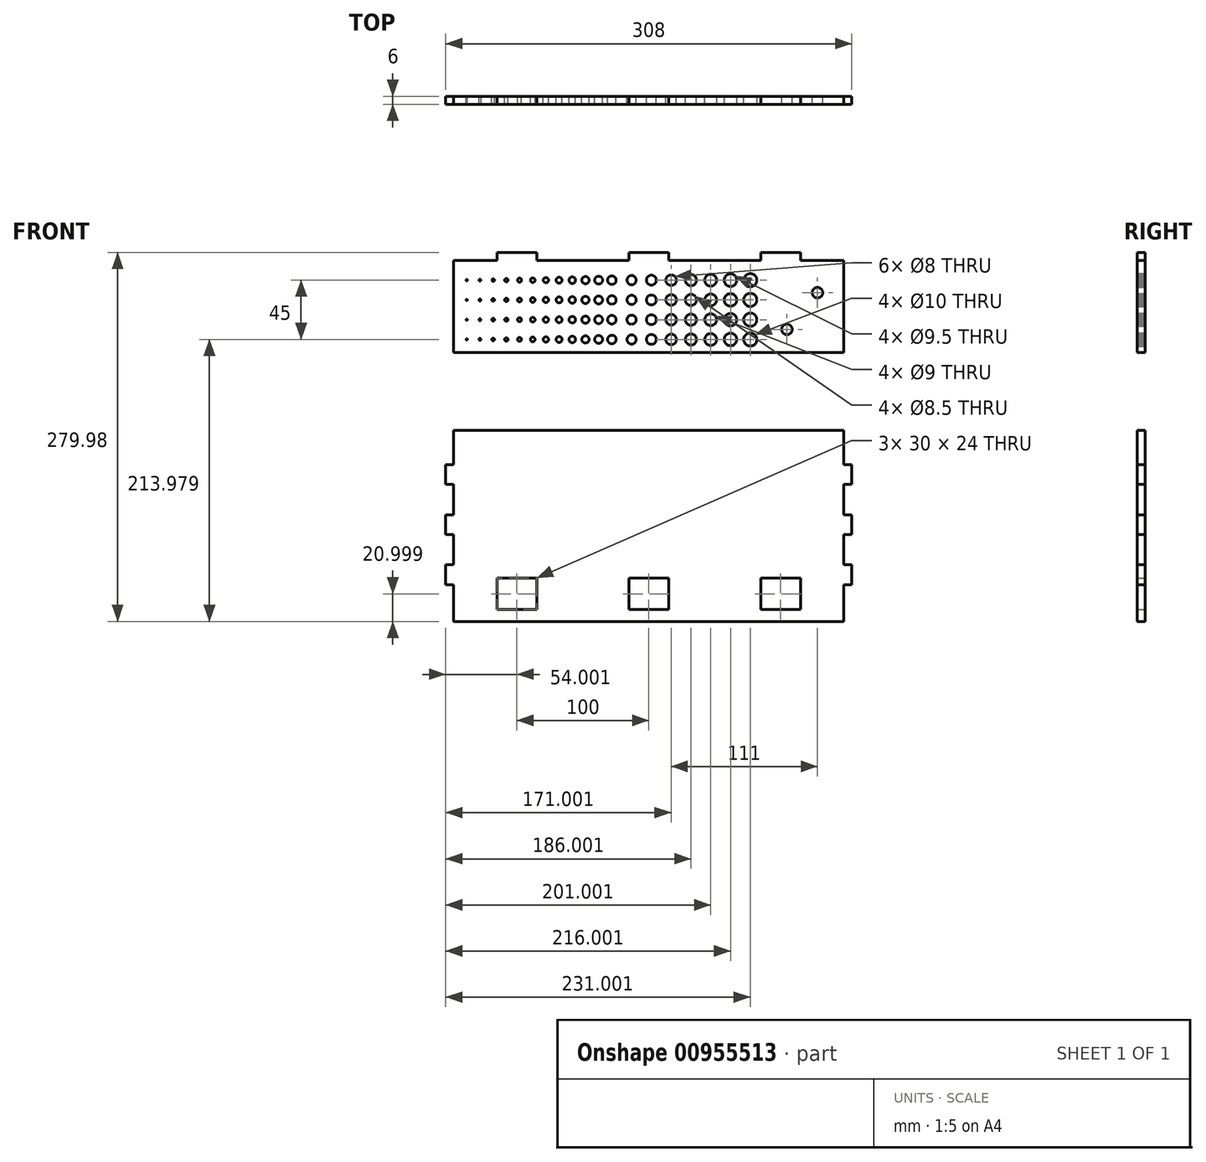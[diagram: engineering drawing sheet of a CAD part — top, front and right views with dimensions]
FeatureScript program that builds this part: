
annotation { "Feature Type Name" : "Feature", "Feature Type Description" : "" }
export const myFeature = defineFeature(function(context is Context, id is Id, definition is map)
    precondition{}
    {
        {
            var Q0;
            Q0=qCreatedBy(makeId("Front.planeOp"),FACE);
            var sketch = newSketch(context, id + "F0", { "sketchPlane" : qUnion([Q0])});
            skLineSegment(sketch, "E0", {"start": v(-100.8, -16.21) * mm, "end": v(195.2, -16.21) * mm, "construction": true});
            skPoint(sketch, "E1", {"position": v(-90.8, -16.21) * mm});
            skPoint(sketch, "E2.1.0.0", {"position": v(-80.8, -16.21) * mm});
            skPoint(sketch, "E2.2.0.0", {"position": v(-70.8, -16.21) * mm});
            skPoint(sketch, "E2.3.0.0", {"position": v(-60.8, -16.21) * mm});
            skPoint(sketch, "E2.4.0.0", {"position": v(-50.8, -16.21) * mm});
            skPoint(sketch, "E2.5.0.0", {"position": v(-40.8, -16.21) * mm});
            skPoint(sketch, "E2.6.0.0", {"position": v(-30.8, -16.21) * mm});
            skPoint(sketch, "E2.7.0.0", {"position": v(-20.8, -16.21) * mm});
            skPoint(sketch, "E2.8.0.0", {"position": v(-10.8, -16.21) * mm});
            skPoint(sketch, "E2.9.0.0", {"position": v(-0.8, -16.21) * mm});
            skPoint(sketch, "E2.10.0.0", {"position": v(9.2, -16.21) * mm});
            skPoint(sketch, "E2.11.0.0", {"position": v(19.2, -16.21) * mm});
            skLineSegment(sketch, "E2.direction1", {"start": v(-90.8, -16.21) * mm, "end": v(-80.8, -16.21) * mm, "construction": true});
            skPoint(sketch, "E3", {"position": v(34.2, -16.21) * mm});
            skPoint(sketch, "E4.1.0.0", {"position": v(49.2, -16.21) * mm});
            skPoint(sketch, "E4.2.0.0", {"position": v(64.2, -16.21) * mm});
            skPoint(sketch, "E4.3.0.0", {"position": v(79.2, -16.21) * mm});
            skPoint(sketch, "E4.4.0.0", {"position": v(94.2, -16.21) * mm});
            skPoint(sketch, "E4.5.0.0", {"position": v(109.2, -16.21) * mm});
            skPoint(sketch, "E4.6.0.0", {"position": v(124.2, -16.21) * mm});
            skLineSegment(sketch, "E4.direction1", {"start": v(34.2, -16.21) * mm, "end": v(49.2, -16.21) * mm, "construction": true});
            skCircle(sketch, "E5", {"center": v(-90.8, -16.21) * mm, "radius": 0.5 * mm});
            skCircle(sketch, "E6", {"center": v(-80.8, -16.21) * mm, "radius": 0.75 * mm});
            skCircle(sketch, "E7", {"center": v(-70.8, -16.21) * mm, "radius": 1 * mm});
            skCircle(sketch, "E8", {"center": v(-60.8, -16.21) * mm, "radius": 1.25 * mm});
            skCircle(sketch, "E9", {"center": v(-50.8, -16.21) * mm, "radius": 1.5 * mm});
            skCircle(sketch, "E10", {"center": v(-40.8, -16.21) * mm, "radius": 1.75 * mm});
            skCircle(sketch, "E11", {"center": v(-30.8, -16.21) * mm, "radius": 2 * mm});
            skCircle(sketch, "E12", {"center": v(-20.8, -16.21) * mm, "radius": 2.25 * mm});
            skCircle(sketch, "E13", {"center": v(-10.8, -16.21) * mm, "radius": 2.5 * mm});
            skCircle(sketch, "E14", {"center": v(-0.8, -16.21) * mm, "radius": 2.75 * mm});
            skCircle(sketch, "E15", {"center": v(9.2, -16.21) * mm, "radius": 3 * mm});
            skCircle(sketch, "E16", {"center": v(19.2, -16.21) * mm, "radius": 3.25 * mm});
            skCircle(sketch, "E17", {"center": v(34.2, -16.21) * mm, "radius": 3.5 * mm});
            skCircle(sketch, "E18", {"center": v(49.2, -16.21) * mm, "radius": 3.75 * mm});
            skCircle(sketch, "E19", {"center": v(64.2, -16.21) * mm, "radius": 4 * mm});
            skCircle(sketch, "E20", {"center": v(79.2, -16.21) * mm, "radius": 4.25 * mm});
            skCircle(sketch, "E21", {"center": v(94.2, -16.21) * mm, "radius": 4.5 * mm});
            skCircle(sketch, "E22", {"center": v(109.2, -16.21) * mm, "radius": 4.75 * mm});
            skCircle(sketch, "E23", {"center": v(124.2, -16.21) * mm, "radius": 5 * mm});
            skCircle(sketch, "E24", {"center": v(175.2, 19.28) * mm, "radius": 4 * mm});
            skCircle(sketch, "E25", {"center": v(175.2, 19.28) * mm, "radius": 15 * mm, "construction": true});
            skPoint(sketch, "E26.0.1.0", {"position": v(-90.8, -1.21) * mm});
            skCircle(sketch, "E26.0.1.1", {"center": v(-80.8, -1.21) * mm, "radius": 0.75 * mm});
            skCircle(sketch, "E26.0.1.2", {"center": v(-70.8, -1.21) * mm, "radius": 1 * mm});
            skCircle(sketch, "E26.0.1.3", {"center": v(-60.8, -1.21) * mm, "radius": 1.25 * mm});
            skCircle(sketch, "E26.0.1.4", {"center": v(-50.8, -1.21) * mm, "radius": 1.5 * mm});
            skCircle(sketch, "E26.0.1.5", {"center": v(-40.8, -1.21) * mm, "radius": 1.75 * mm});
            skCircle(sketch, "E26.0.1.6", {"center": v(-30.8, -1.21) * mm, "radius": 2 * mm});
            skCircle(sketch, "E26.0.1.7", {"center": v(-20.8, -1.21) * mm, "radius": 2.25 * mm});
            skCircle(sketch, "E26.0.1.8", {"center": v(-10.8, -1.21) * mm, "radius": 2.5 * mm});
            skCircle(sketch, "E26.0.1.9", {"center": v(-0.8, -1.21) * mm, "radius": 2.75 * mm});
            skCircle(sketch, "E26.0.1.10", {"center": v(9.2, -1.21) * mm, "radius": 3 * mm});
            skCircle(sketch, "E26.0.1.11", {"center": v(19.2, -1.21) * mm, "radius": 3.25 * mm});
            skCircle(sketch, "E26.0.1.12", {"center": v(34.2, -1.21) * mm, "radius": 3.5 * mm});
            skCircle(sketch, "E26.0.1.13", {"center": v(49.2, -1.21) * mm, "radius": 3.75 * mm});
            skCircle(sketch, "E26.0.1.14", {"center": v(64.2, -1.21) * mm, "radius": 4 * mm});
            skCircle(sketch, "E26.0.1.15", {"center": v(79.2, -1.21) * mm, "radius": 4.25 * mm});
            skCircle(sketch, "E26.0.1.16", {"center": v(94.2, -1.21) * mm, "radius": 4.5 * mm});
            skCircle(sketch, "E26.0.1.17", {"center": v(109.2, -1.21) * mm, "radius": 4.75 * mm});
            skCircle(sketch, "E26.0.1.18", {"center": v(124.2, -1.21) * mm, "radius": 5 * mm});
            skPoint(sketch, "E26.0.2.0", {"position": v(-90.8, 13.79) * mm});
            skCircle(sketch, "E26.0.2.1", {"center": v(-80.8, 13.79) * mm, "radius": 0.75 * mm});
            skCircle(sketch, "E26.0.2.2", {"center": v(-70.8, 13.79) * mm, "radius": 1 * mm});
            skCircle(sketch, "E26.0.2.3", {"center": v(-60.8, 13.79) * mm, "radius": 1.25 * mm});
            skCircle(sketch, "E26.0.2.4", {"center": v(-50.8, 13.79) * mm, "radius": 1.5 * mm});
            skCircle(sketch, "E26.0.2.5", {"center": v(-40.8, 13.79) * mm, "radius": 1.75 * mm});
            skCircle(sketch, "E26.0.2.6", {"center": v(-30.8, 13.79) * mm, "radius": 2 * mm});
            skCircle(sketch, "E26.0.2.7", {"center": v(-20.8, 13.79) * mm, "radius": 2.25 * mm});
            skCircle(sketch, "E26.0.2.8", {"center": v(-10.8, 13.79) * mm, "radius": 2.5 * mm});
            skCircle(sketch, "E26.0.2.9", {"center": v(-0.8, 13.79) * mm, "radius": 2.75 * mm});
            skCircle(sketch, "E26.0.2.10", {"center": v(9.2, 13.79) * mm, "radius": 3 * mm});
            skCircle(sketch, "E26.0.2.11", {"center": v(19.2, 13.79) * mm, "radius": 3.25 * mm});
            skCircle(sketch, "E26.0.2.12", {"center": v(34.2, 13.79) * mm, "radius": 3.5 * mm});
            skCircle(sketch, "E26.0.2.13", {"center": v(49.2, 13.79) * mm, "radius": 3.75 * mm});
            skCircle(sketch, "E26.0.2.14", {"center": v(64.2, 13.79) * mm, "radius": 4 * mm});
            skCircle(sketch, "E26.0.2.15", {"center": v(79.2, 13.79) * mm, "radius": 4.25 * mm});
            skCircle(sketch, "E26.0.2.16", {"center": v(94.2, 13.79) * mm, "radius": 4.5 * mm});
            skCircle(sketch, "E26.0.2.17", {"center": v(109.2, 13.79) * mm, "radius": 4.75 * mm});
            skCircle(sketch, "E26.0.2.18", {"center": v(124.2, 13.79) * mm, "radius": 5 * mm});
            skPoint(sketch, "E26.0.3.0", {"position": v(-90.8, 28.79) * mm});
            skCircle(sketch, "E26.0.3.1", {"center": v(-80.8, 28.79) * mm, "radius": 0.75 * mm});
            skCircle(sketch, "E26.0.3.2", {"center": v(-70.8, 28.79) * mm, "radius": 1 * mm});
            skCircle(sketch, "E26.0.3.3", {"center": v(-60.8, 28.79) * mm, "radius": 1.25 * mm});
            skCircle(sketch, "E26.0.3.4", {"center": v(-50.8, 28.79) * mm, "radius": 1.5 * mm});
            skCircle(sketch, "E26.0.3.5", {"center": v(-40.8, 28.79) * mm, "radius": 1.75 * mm});
            skCircle(sketch, "E26.0.3.6", {"center": v(-30.8, 28.79) * mm, "radius": 2 * mm});
            skCircle(sketch, "E26.0.3.7", {"center": v(-20.8, 28.79) * mm, "radius": 2.25 * mm});
            skCircle(sketch, "E26.0.3.8", {"center": v(-10.8, 28.79) * mm, "radius": 2.5 * mm});
            skCircle(sketch, "E26.0.3.9", {"center": v(-0.8, 28.79) * mm, "radius": 2.75 * mm});
            skCircle(sketch, "E26.0.3.10", {"center": v(9.2, 28.79) * mm, "radius": 3 * mm});
            skCircle(sketch, "E26.0.3.11", {"center": v(19.2, 28.79) * mm, "radius": 3.25 * mm});
            skCircle(sketch, "E26.0.3.12", {"center": v(34.2, 28.79) * mm, "radius": 3.5 * mm});
            skCircle(sketch, "E26.0.3.13", {"center": v(49.2, 28.79) * mm, "radius": 3.75 * mm});
            skCircle(sketch, "E26.0.3.14", {"center": v(64.2, 28.79) * mm, "radius": 4 * mm});
            skCircle(sketch, "E26.0.3.15", {"center": v(79.2, 28.79) * mm, "radius": 4.25 * mm});
            skCircle(sketch, "E26.0.3.16", {"center": v(94.2, 28.79) * mm, "radius": 4.5 * mm});
            skCircle(sketch, "E26.0.3.17", {"center": v(109.2, 28.79) * mm, "radius": 4.75 * mm});
            skCircle(sketch, "E26.0.3.18", {"center": v(124.2, 28.79) * mm, "radius": 5 * mm});
            skLineSegment(sketch, "E26.direction1", {"start": v(-90.8, -16.21) * mm, "end": v(-115.8, -16.21) * mm, "construction": true});
            skLineSegment(sketch, "E26.direction2", {"start": v(-90.8, -16.21) * mm, "end": v(-90.8, -1.21) * mm, "construction": true});
            skLineSegment(sketch, "E27.bottom", {"start": v(195.2, 43.79) * mm, "end": v(162.2, 43.79) * mm});
            skLineSegment(sketch, "E27.top", {"start": v(195.2, -26.21) * mm, "end": v(-100.8, -26.21) * mm});
            skLineSegment(sketch, "E27.left", {"start": v(195.2, 43.79) * mm, "end": v(195.2, -26.21) * mm});
            skLineSegment(sketch, "E27.right", {"start": v(-100.8, 43.79) * mm, "end": v(-100.8, -26.21) * mm});
            skCircle(sketch, "E28", {"center": v(152, -8.55) * mm, "radius": 4 * mm});
            skCircle(sketch, "E29", {"center": v(152, -8.55) * mm, "radius": 15 * mm, "construction": true});
            skLineSegment(sketch, "E30.top", {"start": v(-67.8, 49.79) * mm, "end": v(-37.8, 49.79) * mm});
            skLineSegment(sketch, "E30.left", {"start": v(-67.8, 43.79) * mm, "end": v(-67.8, 49.79) * mm});
            skLineSegment(sketch, "E30.right", {"start": v(-37.8, 43.79) * mm, "end": v(-37.8, 49.79) * mm});
            skLineSegment(sketch, "E31.1.0.0", {"start": v(32.2, 43.79) * mm, "end": v(32.2, 49.79) * mm});
            skLineSegment(sketch, "E31.1.0.1", {"start": v(32.2, 49.79) * mm, "end": v(62.2, 49.79) * mm});
            skLineSegment(sketch, "E31.1.0.2", {"start": v(62.2, 43.79) * mm, "end": v(62.2, 49.79) * mm});
            skLineSegment(sketch, "E31.2.0.0", {"start": v(132.2, 43.79) * mm, "end": v(132.2, 49.79) * mm});
            skLineSegment(sketch, "E31.2.0.1", {"start": v(132.2, 49.79) * mm, "end": v(162.2, 49.79) * mm});
            skLineSegment(sketch, "E31.2.0.2", {"start": v(162.2, 43.79) * mm, "end": v(162.2, 49.79) * mm});
            skLineSegment(sketch, "E31.direction1", {"start": v(-37.8, 43.79) * mm, "end": v(32.2, 43.79) * mm, "construction": true});
            skLineSegment(sketch, "E32.trimOffspring", {"start": v(32.2, 43.79) * mm, "end": v(-37.8, 43.79) * mm});
            skLineSegment(sketch, "E33.trimOffspring", {"start": v(-67.8, 43.79) * mm, "end": v(-100.8, 43.79) * mm});
            skLineSegment(sketch, "E34.trimOffspring", {"start": v(132.2, 43.79) * mm, "end": v(62.2, 43.79) * mm});
            skLineSegment(sketch, "E35.bottom", {"start": v(-100.8, -85.2) * mm, "end": v(195.2, -85.2) * mm});
            skLineSegment(sketch, "E35.top", {"start": v(-100.8, -230.2) * mm, "end": v(195.2, -230.2) * mm});
            skLineSegment(sketch, "E35.left", {"start": v(-100.8, -85.2) * mm, "end": v(-100.8, -111.2) * mm});
            skLineSegment(sketch, "E35.right", {"start": v(195.2, -85.2) * mm, "end": v(195.2, -111.2) * mm});
            skLineSegment(sketch, "E36", {"start": v(-100.8, -197.2) * mm, "end": v(195.2, -197.2) * mm, "construction": true});
            skLineSegment(sketch, "E37.bottom", {"start": v(-67.8, -197.2) * mm, "end": v(-37.8, -197.2) * mm});
            skLineSegment(sketch, "E37.top", {"start": v(-67.8, -221.2) * mm, "end": v(-37.8, -221.2) * mm});
            skLineSegment(sketch, "E37.left", {"start": v(-67.8, -197.2) * mm, "end": v(-67.8, -221.2) * mm});
            skLineSegment(sketch, "E37.right", {"start": v(-37.8, -197.2) * mm, "end": v(-37.8, -221.2) * mm});
            skLineSegment(sketch, "E38.1.0.0", {"start": v(32.2, -197.2) * mm, "end": v(32.2, -221.2) * mm});
            skLineSegment(sketch, "E38.1.0.1", {"start": v(62.2, -197.2) * mm, "end": v(62.2, -221.2) * mm});
            skLineSegment(sketch, "E38.1.0.2", {"start": v(32.2, -221.2) * mm, "end": v(62.2, -221.2) * mm});
            skLineSegment(sketch, "E38.1.0.3", {"start": v(32.2, -197.2) * mm, "end": v(62.2, -197.2) * mm});
            skLineSegment(sketch, "E38.2.0.0", {"start": v(132.2, -197.2) * mm, "end": v(132.2, -221.2) * mm});
            skLineSegment(sketch, "E38.2.0.1", {"start": v(162.2, -197.2) * mm, "end": v(162.2, -221.2) * mm});
            skLineSegment(sketch, "E38.2.0.2", {"start": v(132.2, -221.2) * mm, "end": v(162.2, -221.2) * mm});
            skLineSegment(sketch, "E38.2.0.3", {"start": v(132.2, -197.2) * mm, "end": v(162.2, -197.2) * mm});
            skLineSegment(sketch, "E38.direction1", {"start": v(-67.8, -221.2) * mm, "end": v(32.2, -221.2) * mm, "construction": true});
            skLineSegment(sketch, "E39.bottom", {"start": v(-100.8, -111.2) * mm, "end": v(-106.8, -111.2) * mm});
            skLineSegment(sketch, "E39.top", {"start": v(-100.8, -126.2) * mm, "end": v(-106.8, -126.2) * mm});
            skLineSegment(sketch, "E39.right", {"start": v(-106.8, -111.2) * mm, "end": v(-106.8, -126.2) * mm});
            skLineSegment(sketch, "E40.0.1.0", {"start": v(-100.8, -149.2) * mm, "end": v(-106.8, -149.2) * mm});
            skLineSegment(sketch, "E40.0.1.1", {"start": v(-106.8, -149.2) * mm, "end": v(-106.8, -164.2) * mm});
            skLineSegment(sketch, "E40.0.1.2", {"start": v(-100.8, -164.2) * mm, "end": v(-106.8, -164.2) * mm});
            skLineSegment(sketch, "E40.1.0.0", {"start": v(201.2, -111.2) * mm, "end": v(195.2, -111.2) * mm});
            skLineSegment(sketch, "E40.1.0.2", {"start": v(201.2, -126.2) * mm, "end": v(195.2, -126.2) * mm});
            skLineSegment(sketch, "E40.1.0.3", {"start": v(201.2, -111.2) * mm, "end": v(201.2, -126.2) * mm});
            skLineSegment(sketch, "E40.1.1.0", {"start": v(201.2, -149.2) * mm, "end": v(195.2, -149.2) * mm});
            skLineSegment(sketch, "E40.1.1.2", {"start": v(201.2, -164.2) * mm, "end": v(195.2, -164.2) * mm});
            skLineSegment(sketch, "E40.1.1.3", {"start": v(201.2, -149.2) * mm, "end": v(201.2, -164.2) * mm});
            skLineSegment(sketch, "E40.direction1", {"start": v(-106.8, -111.2) * mm, "end": v(195.2, -111.2) * mm, "construction": true});
            skLineSegment(sketch, "E40.direction2", {"start": v(-106.8, -111.2) * mm, "end": v(-106.8, -149.2) * mm, "construction": true});
            skLineSegment(sketch, "E41.0.0.2", {"start": v(-100.8, -187.2) * mm, "end": v(-106.8, -187.2) * mm});
            skLineSegment(sketch, "E41.3.0.2", {"start": v(-106.8, -187.2) * mm, "end": v(-106.8, -202.2) * mm});
            skLineSegment(sketch, "E41.6.0.2", {"start": v(-100.8, -202.2) * mm, "end": v(-106.8, -202.2) * mm});
            skLineSegment(sketch, "E41.0.1.2", {"start": v(201.2, -187.2) * mm, "end": v(195.2, -187.2) * mm});
            skLineSegment(sketch, "E41.6.1.2", {"start": v(201.2, -202.2) * mm, "end": v(195.2, -202.2) * mm});
            skLineSegment(sketch, "E41.9.1.2", {"start": v(201.2, -187.2) * mm, "end": v(201.2, -202.2) * mm});
            skLineSegment(sketch, "E42.trimOffspring", {"start": v(-100.8, -126.2) * mm, "end": v(-100.8, -149.2) * mm});
            skLineSegment(sketch, "E43.trimOffspring", {"start": v(-100.8, -164.2) * mm, "end": v(-100.8, -187.2) * mm});
            skLineSegment(sketch, "E44.trimOffspring", {"start": v(-100.8, -202.2) * mm, "end": v(-100.8, -230.2) * mm});
            skLineSegment(sketch, "E45.trimOffspring", {"start": v(195.2, -202.2) * mm, "end": v(195.2, -230.2) * mm});
            skLineSegment(sketch, "E46.trimOffspring", {"start": v(195.2, -164.2) * mm, "end": v(195.2, -187.2) * mm});
            skLineSegment(sketch, "E47.trimOffspring", {"start": v(195.2, -126.2) * mm, "end": v(195.2, -149.2) * mm});
            skCircle(sketch, "E48.0.1.0", {"center": v(-90.8, -1.21) * mm, "radius": 0.5 * mm});
            skCircle(sketch, "E48.0.2.0", {"center": v(-90.8, 13.79) * mm, "radius": 0.5 * mm});
            skCircle(sketch, "E48.0.3.0", {"center": v(-90.8, 28.79) * mm, "radius": 0.5 * mm});
            skLineSegment(sketch, "E48.direction1", {"start": v(-90.8, -16.21) * mm, "end": v(-65.8, -16.21) * mm, "construction": true});
            skSolve(sketch);
        }
        {
            var Q0;
            Q0=makeQuery(id+"F0.imprint","IMPRINT",FACE,{"disambiguationData":[TD([[makeQuery(id+"F0.imprint","IMPRINT",EDGE,{"derivedFrom":sQuery(id+"F0.wireOp",EDGE,"E35.bottom")}),-1.0]])]});
            var Q1;
            Q1=makeQuery(id+"F0.imprint","IMPRINT",FACE,{"disambiguationData":[TD([[makeQuery(id+"F0.imprint","IMPRINT",EDGE,{"derivedFrom":sQuery(id+"F0.wireOp",EDGE,"E5")}),-1.0]])]});
            extrude(context, id + "F1", {"entities" : qUnion([Q0, Q1]), "depth" : 6 * mm, "offsetDistance" : 25 * mm});
        }
    });
